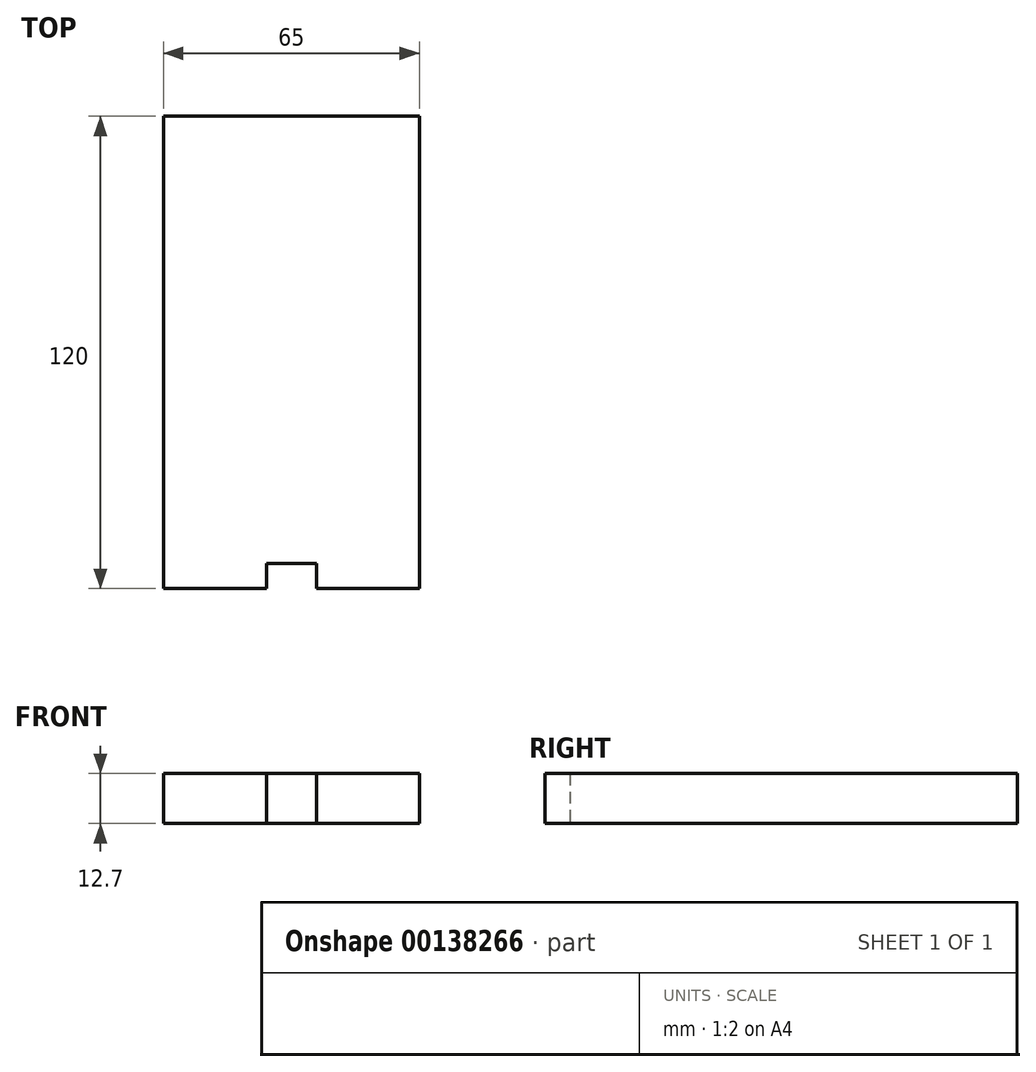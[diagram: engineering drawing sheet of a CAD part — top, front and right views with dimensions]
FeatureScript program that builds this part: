
annotation { "Feature Type Name" : "Feature", "Feature Type Description" : "" }
export const myFeature = defineFeature(function(context is Context, id is Id, definition is map)
    precondition{}
    {
        {
            var Q0;
            Q0=qCreatedBy(makeId("Top.planeOp"),FACE);
            var sketch = newSketch(context, id + "F0", { "sketchPlane" : qUnion([Q0])});
            skLineSegment(sketch, "E0.bottom", {"start": v(-32.5, -60) * mm, "end": v(32.5, -60) * mm});
            skLineSegment(sketch, "E0.top", {"start": v(-32.5, 60) * mm, "end": v(32.5, 60) * mm});
            skLineSegment(sketch, "E0.left", {"start": v(-32.5, -60) * mm, "end": v(-32.5, 60) * mm});
            skLineSegment(sketch, "E0.right", {"start": v(32.5, -60) * mm, "end": v(32.5, 60) * mm});
            skPoint(sketch, "E0.middle", {"position": v(0, 0) * mm});
            skLineSegment(sketch, "E1.bottom", {"start": v(6.35, -60) * mm, "end": v(-6.35, -60) * mm});
            skLineSegment(sketch, "E1.top", {"start": v(6.35, -53.65) * mm, "end": v(-6.35, -53.65) * mm});
            skLineSegment(sketch, "E1.left", {"start": v(6.35, -60) * mm, "end": v(6.35, -53.65) * mm});
            skLineSegment(sketch, "E1.right", {"start": v(-6.35, -60) * mm, "end": v(-6.35, -53.65) * mm});
            skPoint(sketch, "E1.middle", {"position": v(0, -56.83) * mm});
            skPoint(sketch, "E1.middle.positionSnap0", {"position": v(0, -60) * mm});
            skPoint(sketch, "E1.centerSnap0", {"position": v(0, -60) * mm});
            skSolve(sketch);
        }
        {
            var Q0;
            Q0=makeQuery(id+"F0.imprint","IMPRINT",FACE,{"disambiguationData":[TD([[makeQuery(id+"F0.imprint","IMPRINT",EDGE,{"derivedFrom":sQuery(id+"F0.wireOp",EDGE,"E0.bottom")}),1.0]])]});
            extrude(context, id + "F1", {"entities" : qUnion([Q0]), "depth" : 12.7 * mm});
        }
    });
